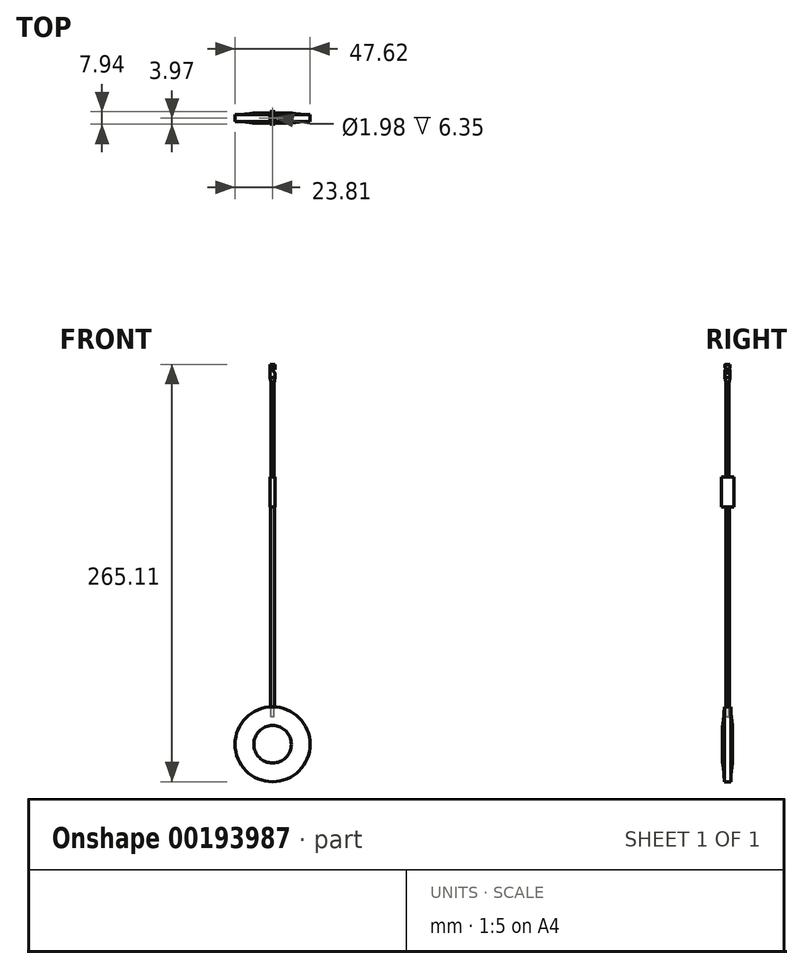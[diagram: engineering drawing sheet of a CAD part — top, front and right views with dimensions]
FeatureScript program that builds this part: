
annotation { "Feature Type Name" : "Feature", "Feature Type Description" : "" }
export const myFeature = defineFeature(function(context is Context, id is Id, definition is map)
    precondition{}
    {
        {
            var Q0;
            Q0=qCreatedBy(makeId("Top.planeOp"),FACE);
            var sketch = newSketch(context, id + "F0", { "sketchPlane" : qUnion([Q0])});
            skCircle(sketch, "E0", {"center": v(0, 0) * mm, "radius": 1.59 * mm});
            skSolve(sketch);
        }
        {
            var Q0;
            Q0=makeQuery(id+"F0.imprint","IMPRINT",FACE,{"disambiguationData":[TD([[makeQuery(id+"F0.imprint","IMPRINT",EDGE,{"derivedFrom":sQuery(id+"F0.wireOp",EDGE,"E0")}),1.0]])]});
            extrude(context, id + "F1", {"entities" : qUnion([Q0]), "oppositeDirection" : true, "depth" : 11.1 * mm});
        }
        {
            var Q0;
            Q0=makeQuery(id+"F1.opExtrude","CAP_EDGE",EDGE,{"disambiguationData":[OSD([sQuery(id+"F0.wireOp",EDGE,"E0")])],"isStart":false});
            chamfer(context, id + "F2", {"entities" : qUnion([Q0]), "chamferType" : ChamferType.OFFSET_ANGLE, "width" : 0.5 * mm, "oppositeDirection" : true, "angle" : 80 * degree, "tangentPropagation" : true});
        }
        {
            var Q0;
            Q0=makeQuery(id+"F1.opExtrude","CAP_FACE",FACE,{"disambiguationData":[OSD([sQuery(id+"F0.wireOp",EDGE,"E0")])],"isStart":false});
            var sketch = newSketch(context, id + "F3", { "sketchPlane" : qUnion([Q0])});
            skCircle(sketch, "E1", {"center": v(0, 0) * mm, "radius": 1 * mm});
            skSolve(sketch);
        }
        {
            var Q0;
            Q0=makeQuery(id+"F3.imprint","IMPRINT",FACE,{"disambiguationData":[TD([[makeQuery(id+"F3.imprint","IMPRINT",EDGE,{"derivedFrom":sQuery(id+"F3.wireOp",EDGE,"E1")}),1.0]])]});
            extrude(context, id + "F4", {"entities" : qUnion([Q0]), "depth" : 60.32 * mm});
        }
        {
            var Q0;
            Q0=makeQuery(id+"F4.opExtrude","CAP_FACE",FACE,{"disambiguationData":[OSD([sQuery(id+"F3.wireOp",EDGE,"E1")])],"isStart":false});
            var sketch = newSketch(context, id + "F5", { "sketchPlane" : qUnion([Q0])});
            skLineSegment(sketch, "E2.bottom", {"start": v(-1.59, 3.97) * mm, "end": v(1.59, 3.97) * mm});
            skLineSegment(sketch, "E2.top", {"start": v(-1.59, -3.97) * mm, "end": v(1.59, -3.97) * mm});
            skLineSegment(sketch, "E2.left", {"start": v(-1.59, 3.97) * mm, "end": v(-1.59, -3.97) * mm});
            skLineSegment(sketch, "E2.right", {"start": v(1.59, 3.97) * mm, "end": v(1.59, -3.97) * mm});
            skPoint(sketch, "E2.middle", {"position": v(0, 0) * mm});
            skSolve(sketch);
        }
        {
            var Q0;
            Q0 = qSketchRegion(id + "F5", true);
            extrude(context, id + "F6", {"entities" : qUnion([Q0]), "depth" : 19.05 * mm});
        }
        {
            var Q0;
            Q0=makeQuery(id+"F6.opExtrude","CAP_FACE",FACE,{"disambiguationData":[OSD([sQuery(id+"F5.wireOp",EDGE,"E2.bottom"),sQuery(id+"F5.wireOp",EDGE,"E2.top"),sQuery(id+"F5.wireOp",EDGE,"E2.left"),sQuery(id+"F5.wireOp",EDGE,"E2.right")])],"isStart":false});
            var sketch = newSketch(context, id + "F7", { "sketchPlane" : qUnion([Q0])});
            skCircle(sketch, "E3", {"center": v(0, 0) * mm, "radius": 1.2 * mm});
            skSolve(sketch);
        }
        {
            var Q0;
            Q0=makeQuery(id+"F7.imprint","IMPRINT",FACE,{"disambiguationData":[TD([[makeQuery(id+"F7.imprint","IMPRINT",EDGE,{"derivedFrom":sQuery(id+"F7.wireOp",EDGE,"E3")}),1.0]])]});
            extrude(context, id + "F8", {"entities" : qUnion([Q0]), "depth" : 127 * mm});
        }
        {
            var Q0;
            Q0=qCreatedBy(makeId("Front.planeOp"),FACE);
            var sketch = newSketch(context, id + "F9", { "sketchPlane" : qUnion([Q0])});
            skCircle(sketch, "E4", {"center": v(0, -2.74) * mm, "radius": 0.82 * mm});
            skLineSegment(sketch, "E5", {"start": v(0, 0) * mm, "end": v(0, -8.23) * mm, "construction": true});
            skLineSegment(sketch, "E6", {"start": v(0.58, -2.17) * mm, "end": v(1.85, -3.44) * mm});
            skLineSegment(sketch, "E7", {"start": v(-0.58, -3.32) * mm, "end": v(1.85, -5.75) * mm});
            skLineSegment(sketch, "E8", {"start": v(1.85, -3.44) * mm, "end": v(1.85, -5.75) * mm});
            skSolve(sketch);
        }
        {
            var Q0;
            Q0 = qSketchRegion(id + "F9", true);
            extrude(context, id + "F10", {"entities" : qUnion([Q0]), "operationType" : NewBodyOperationType.REMOVE, "oppositeDirection" : true, "depth" : 6.35 * mm, "symmetric" : true});
        }
        {
            var Q0;
            Q0=qCreatedBy(makeId("Right.planeOp"),FACE);
            var sketch = newSketch(context, id + "F11", { "sketchPlane" : qUnion([Q0])});
            skLineSegment(sketch, "E9", {"start": v(0, -217.49) * mm, "end": v(0, -241.3) * mm, "construction": true});
            skLineSegment(sketch, "E10", {"start": v(-2.08, -217.49) * mm, "end": v(2.08, -217.49) * mm});
            skLineSegment(sketch, "E11", {"start": v(-3.18, -229.4) * mm, "end": v(-3.17, -241.3) * mm});
            skLineSegment(sketch, "E12", {"start": v(-3.17, -241.3) * mm, "end": v(3.17, -241.3) * mm});
            skLineSegment(sketch, "E13", {"start": v(3.18, -241.3) * mm, "end": v(3.18, -229.4) * mm});
            skArc(sketch, "E14", {"start": v(-3.17, -229.4) * mm, "mid": v(-2.36, -223.47) * mm, "end": v(-2.08, -217.49) * mm});
            skArc(sketch, "E15", {"start": v(2.08, -217.49) * mm, "mid": v(2.36, -223.47) * mm, "end": v(3.17, -229.4) * mm});
            skLineSegment(sketch, "E16", {"start": v(2.08, -217.49) * mm, "end": v(2.08, -241.3) * mm, "construction": true});
            skLineSegment(sketch, "E17", {"start": v(-2.08, -217.49) * mm, "end": v(-2.08, -241.3) * mm, "construction": true});
            skLineSegment(sketch, "E18", {"start": v(-3.17, -229.4) * mm, "end": v(3.17, -229.4) * mm, "construction": true});
            skPoint(sketch, "E19", {"position": v(0, -229.4) * mm});
            skSolve(sketch);
        }
        {
            var Q0;
            Q0 = qSketchRegion(id + "F11", true);
            var Q1;
            Q1=sQuery(id+"F11.wireOp",EDGE,"E12");
            revolve(context, id + "F12", {"entities" : qUnion([Q0]), "axis" : qUnion([Q1]), "revolveType" : RevolveType.FULL});
        }
        {
            var Q0;
            Q0=makeQuery(id+"F8.opExtrude","CAP_FACE",FACE,{"disambiguationData":[OSD([sQuery(id+"F7.wireOp",EDGE,"E3")])],"isStart":false});
            cPlane(context, id + "F13", {"entities" : qUnion([Q0]), "cplaneType" : CPlaneType.OFFSET, "offset" : 0 * mm, "oppositeDirection" : true, "width" : 152.4 * mm, "height" : 152.4 * mm});
        }
        {
            var Q0;
            Q0=qCreatedBy(id+"F13.planeOp",FACE);
            var sketch = newSketch(context, id + "F14", { "sketchPlane" : qUnion([Q0])});
            skCircle(sketch, "E20", {"center": v(0, 0) * mm, "radius": 1 * mm});
            skSolve(sketch);
        }
        {
            var Q0;
            Q0=makeQuery(id+"F14.imprint","IMPRINT",FACE,{"disambiguationData":[TD([[makeQuery(id+"F14.imprint","IMPRINT",EDGE,{"derivedFrom":sQuery(id+"F14.wireOp",EDGE,"E20")}),1.0]])]});
            extrude(context, id + "F15", {"entities" : qUnion([Q0]), "operationType" : NewBodyOperationType.REMOVE, "depth" : 6.35 * mm});
        }
    });
